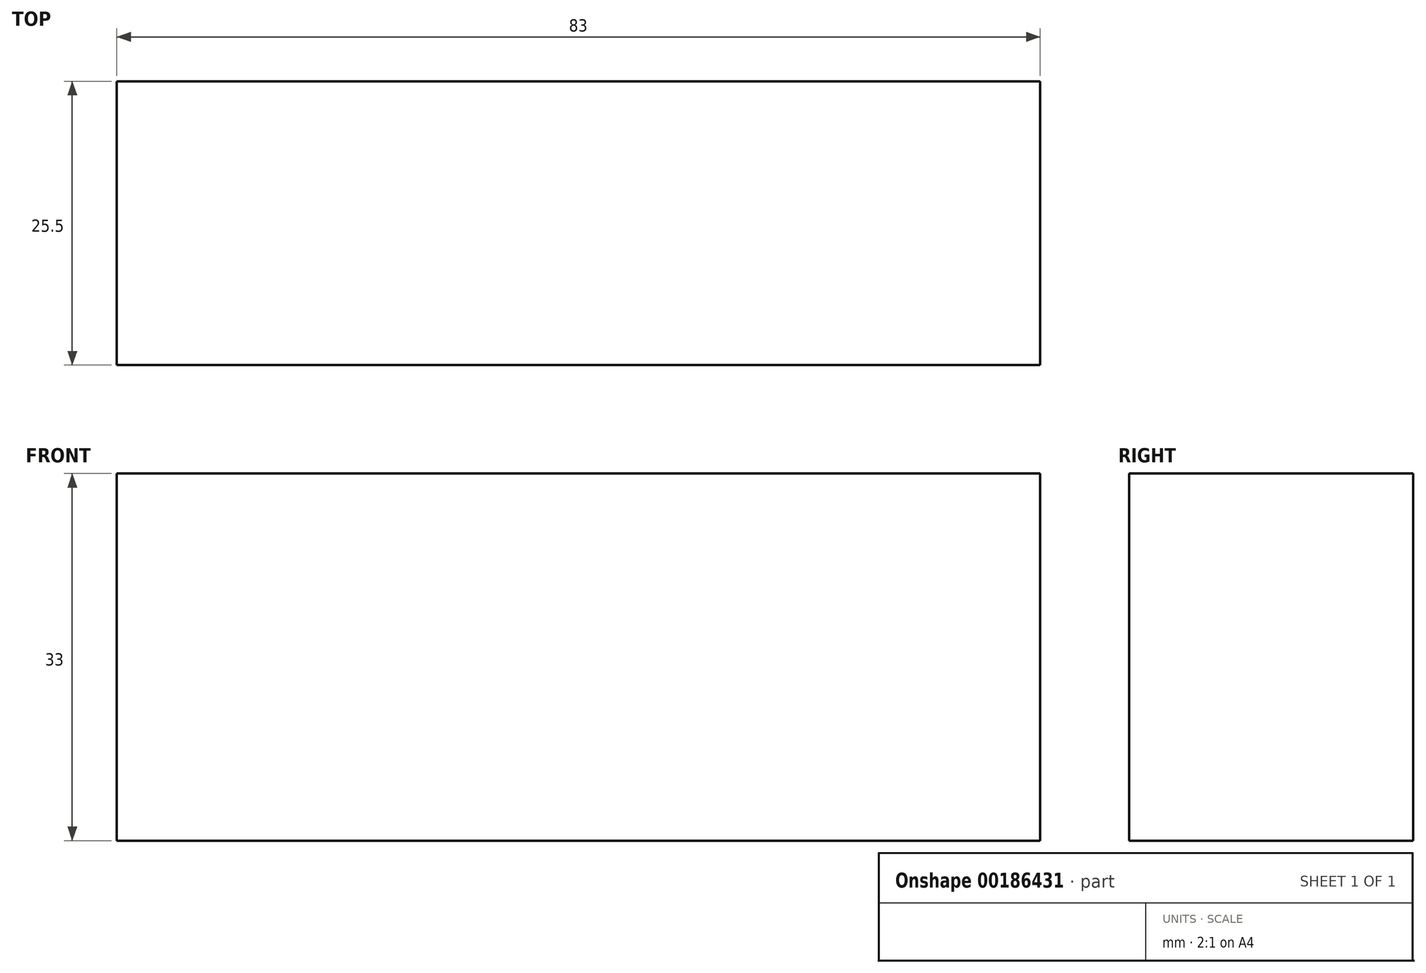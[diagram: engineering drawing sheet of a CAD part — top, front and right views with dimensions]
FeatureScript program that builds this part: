
annotation { "Feature Type Name" : "Feature", "Feature Type Description" : "" }
export const myFeature = defineFeature(function(context is Context, id is Id, definition is map)
    precondition{}
    {
        {
            var Q0;
            Q0=qCreatedBy(makeId("Front.planeOp"),FACE);
            var sketch = newSketch(context, id + "F0", { "sketchPlane" : qUnion([Q0])});
            skLineSegment(sketch, "E0.bottom", {"start": v(-40.36, 9.34) * mm, "end": v(42.64, 9.34) * mm});
            skLineSegment(sketch, "E0.top", {"start": v(-40.36, -23.66) * mm, "end": v(42.64, -23.66) * mm});
            skLineSegment(sketch, "E0.left", {"start": v(-40.36, 9.34) * mm, "end": v(-40.36, -23.66) * mm});
            skLineSegment(sketch, "E0.right", {"start": v(42.64, 9.34) * mm, "end": v(42.64, -23.66) * mm});
            skSolve(sketch);
        }
        {
            var Q0;
            Q0 = qSketchRegion(id + "F0", true);
            extrude(context, id + "F1", {"entities" : qUnion([Q0]), "depth" : 25.5 * mm});
        }
    });
